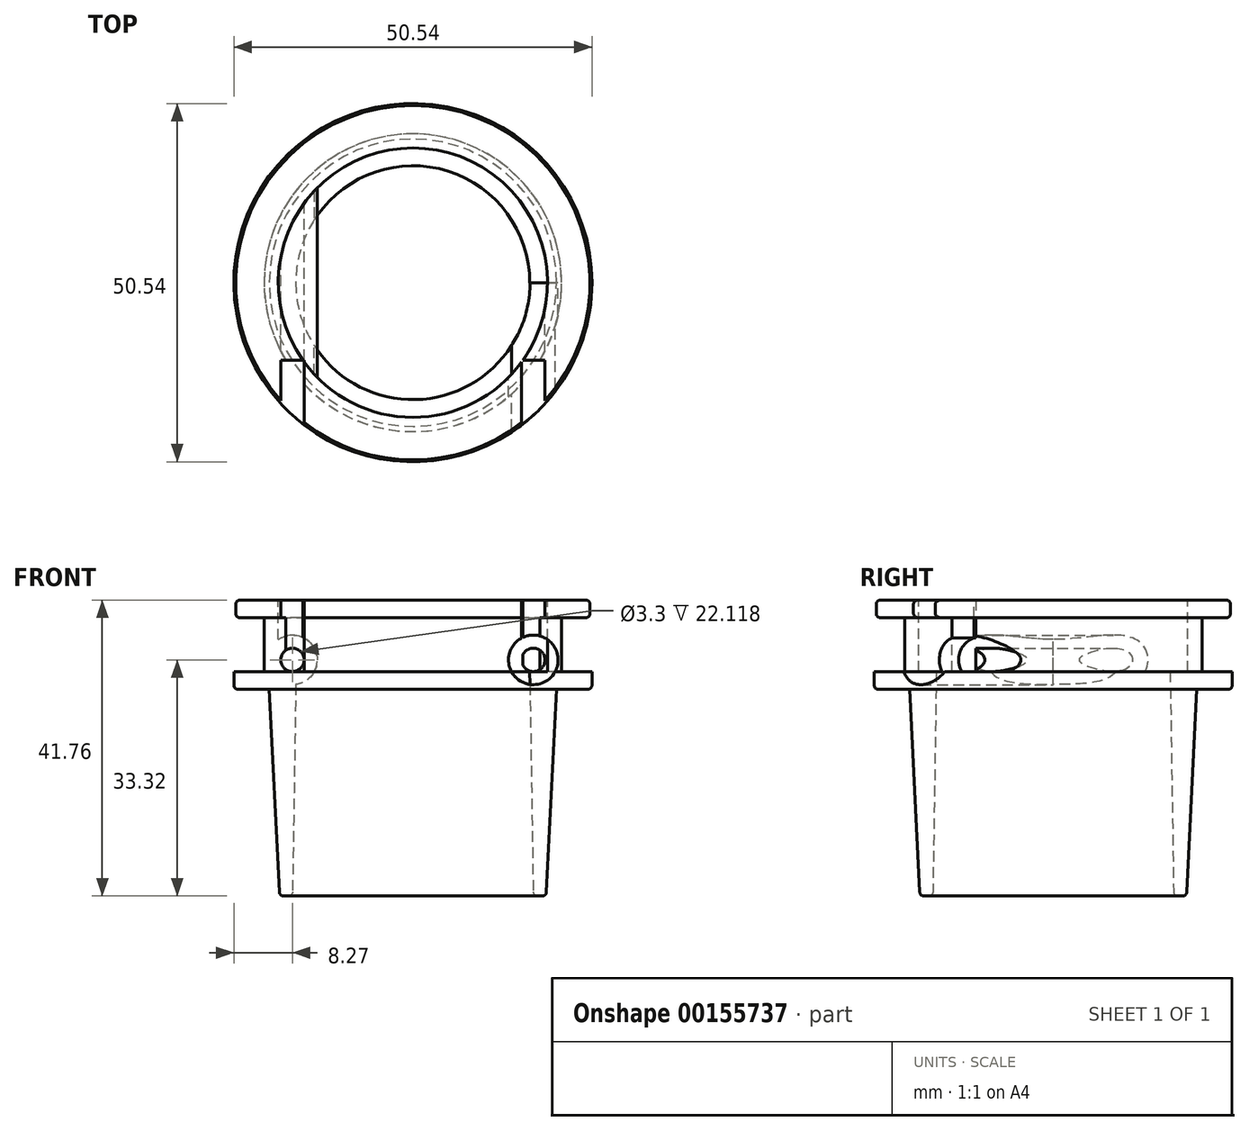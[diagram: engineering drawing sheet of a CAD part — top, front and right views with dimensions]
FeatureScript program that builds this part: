
annotation { "Feature Type Name" : "Feature", "Feature Type Description" : "" }
export const myFeature = defineFeature(function(context is Context, id is Id, definition is map)
    precondition{}
    {
        {
            var Q0;
            Q0=qCreatedBy(makeId("Front.planeOp"),FACE);
            var sketch = newSketch(context, id + "F0", { "sketchPlane" : qUnion([Q0])});
            skLineSegment(sketch, "E0", {"start": v(17, -31.67) * mm, "end": v(18.82, -31.67) * mm});
            skLineSegment(sketch, "E1", {"start": v(17, -31.67) * mm, "end": v(16.5, 0) * mm});
            skLineSegment(sketch, "E2", {"start": v(18.82, -31.67) * mm, "end": v(20.27, -2.5) * mm});
            skLineSegment(sketch, "E3", {"start": v(20.27, -2.5) * mm, "end": v(25.27, -2.5) * mm});
            skLineSegment(sketch, "E4", {"start": v(25.27, -2.5) * mm, "end": v(25.27, 0) * mm});
            skLineSegment(sketch, "E5", {"start": v(25.27, 0) * mm, "end": v(21, 0) * mm});
            skLineSegment(sketch, "E6", {"start": v(19, 0) * mm, "end": v(19, 10.1) * mm});
            skLineSegment(sketch, "E7", {"start": v(19, 10.1) * mm, "end": v(25, 10.1) * mm});
            skLineSegment(sketch, "E8", {"start": v(25, 10.1) * mm, "end": v(25, 7.6) * mm});
            skLineSegment(sketch, "E9", {"start": v(25, 7.6) * mm, "end": v(21, 7.6) * mm});
            skLineSegment(sketch, "E10", {"start": v(21, 7.6) * mm, "end": v(21, 0) * mm});
            skLineSegment(sketch, "E11.trimOffspring", {"start": v(19, 0) * mm, "end": v(16.5, 0) * mm});
            skLineSegment(sketch, "E12", {"start": v(0, 0) * mm, "end": v(0, -100.55) * mm, "construction": true});
            skSolve(sketch);
        }
        {
            var Q0;
            Q0 = qSketchRegion(id + "F0", true);
            var Q1;
            Q1=sQuery(id+"F0.wireOp",EDGE,"E12");
            revolve(context, id + "F1", {"entities" : qUnion([Q0]), "axis" : qUnion([Q1]), "revolveType" : RevolveType.FULL});
        }
        {
            var Q0;
            Q0=qCreatedBy(makeId("Front.planeOp"),FACE);
            var sketch = newSketch(context, id + "F2", { "sketchPlane" : qUnion([Q0])});
            skCircle(sketch, "E13", {"center": v(-17, 1.65) * mm, "radius": 1.65 * mm});
            skCircle(sketch, "E14", {"center": v(-17, 1.65) * mm, "radius": 3.5 * mm});
            skCircle(sketch, "E15.MirrorC", {"center": v(17, 1.65) * mm, "radius": 3.5 * mm});
            skCircle(sketch, "E16.MirrorC", {"center": v(17, 1.65) * mm, "radius": 1.65 * mm});
            skSolve(sketch);
        }
        {
            var Q0;
            Q0=makeQuery(id+"F2.imprint","IMPRINT",FACE,{"disambiguationData":[TD([[makeQuery(id+"F2.imprint","IMPRINT",EDGE,{"derivedFrom":sQuery(id+"F2.wireOp",EDGE,"E13")}),-1.0]])]});
            var Q1;
            Q1=makeQuery(id+"F2.imprint","IMPRINT",FACE,{"disambiguationData":[TD([[makeQuery(id+"F2.imprint","IMPRINT",EDGE,{"derivedFrom":sQuery(id+"F2.wireOp",EDGE,"E15.MirrorC")}),-1.0]])]});
            var Q2;
            Q2=makeQuery(id+"F1.opRevolve","SWEPT_FACE",FACE,{"disambiguationData":[OSD([sQuery(id+"F0.wireOp",EDGE,"E6")])]});
            var Q3;
            Q3=makeQuery(id+"F1.opRevolve","SWEPT_BODY",BODY,{"disambiguationData":[OSD([sQuery(id+"F0.wireOp",EDGE,"E0"),sQuery(id+"F0.wireOp",EDGE,"E1"),sQuery(id+"F0.wireOp",EDGE,"E2"),sQuery(id+"F0.wireOp",EDGE,"E3"),sQuery(id+"F0.wireOp",EDGE,"E4"),sQuery(id+"F0.wireOp",EDGE,"E5"),sQuery(id+"F0.wireOp",EDGE,"E6"),sQuery(id+"F0.wireOp",EDGE,"E7"),sQuery(id+"F0.wireOp",EDGE,"E8"),sQuery(id+"F0.wireOp",EDGE,"E9"),sQuery(id+"F0.wireOp",EDGE,"E10"),sQuery(id+"F0.wireOp",EDGE,"E11.trimOffspring")])]});
            extrude(context, id + "F3", {"entities" : qUnion([Q0, Q1]), "operationType" : NewBodyOperationType.ADD, "endBound" : BoundingType.UP_TO_SURFACE, "endBoundEntityFace" : qUnion([Q2]), "endBoundEntityBody" : qUnion([Q3]), "depth" : 25 * mm});
        }
        {
            var Q0;
            Q0=makeQuery(id+"F2.imprint","IMPRINT",FACE,{"disambiguationData":[TD([[makeQuery(id+"F2.imprint","IMPRINT",EDGE,{"derivedFrom":sQuery(id+"F2.wireOp",EDGE,"E13")}),-1.0]])]});
            var Q1;
            Q1=makeQuery(id+"F2.imprint","IMPRINT",FACE,{"disambiguationData":[TD([[makeQuery(id+"F2.imprint","IMPRINT",EDGE,{"derivedFrom":sQuery(id+"F2.wireOp",EDGE,"E15.MirrorC")}),-1.0]])]});
            var Q2;
            Q2=makeQuery(id+"F3.boolean.opBoolean","SPLIT",FACE,{"disambiguationData":[TD([makeQuery(id+"F1.opRevolve","SWEPT_FACE",FACE,{"disambiguationData":[OSD([sQuery(id+"F0.wireOp",EDGE,"E7")])]})])],"derivedFrom":makeQuery(id+"F1.opRevolve","SWEPT_FACE",FACE,{"disambiguationData":[OSD([sQuery(id+"F0.wireOp",EDGE,"E6")])]})});
            extrude(context, id + "F4", {"entities" : qUnion([Q0, Q1]), "operationType" : NewBodyOperationType.ADD, "endBound" : BoundingType.UP_TO_SURFACE, "oppositeDirection" : true, "endBoundEntityFace" : qUnion([Q2]), "depth" : 25 * mm});
        }
        {
            var Q0;
            Q0=qCreatedBy(makeId("Front.planeOp"),FACE);
            cPlane(context, id + "F5", {"entities" : qUnion([Q0]), "cplaneType" : CPlaneType.OFFSET, "offset" : (21.84 / 2) * mm, "width" : 150 * mm, "height" : 150 * mm});
        }
        {
            var Q0;
            Q0=qCreatedBy(id+"F5.planeOp",FACE);
            var sketch = newSketch(context, id + "F6", { "sketchPlane" : qUnion([Q0])});
            skLineSegment(sketch, "E17.bottom", {"start": v(-18.65, 10.1) * mm, "end": v(-15.35, 10.1) * mm});
            skLineSegment(sketch, "E17.top", {"start": v(-18.65, 0) * mm, "end": v(-15.35, 0) * mm});
            skLineSegment(sketch, "E17.left", {"start": v(-18.65, 10.1) * mm, "end": v(-18.65, 0) * mm});
            skLineSegment(sketch, "E17.right", {"start": v(-15.35, 10.1) * mm, "end": v(-15.35, 0) * mm});
            skLineSegment(sketch, "E18.MirrorCS", {"start": v(18.65, 10.1) * mm, "end": v(18.65, 0) * mm});
            skLineSegment(sketch, "E19.MirrorCS", {"start": v(18.65, 0) * mm, "end": v(15.35, 0) * mm});
            skLineSegment(sketch, "E20.MirrorCS", {"start": v(15.35, 10.1) * mm, "end": v(15.35, 0) * mm});
            skLineSegment(sketch, "E21.MirrorCS", {"start": v(18.65, 10.1) * mm, "end": v(15.35, 10.1) * mm});
            skSolve(sketch);
        }
        {
            var Q0;
            Q0 = qSketchRegion(id + "F6", true);
            extrude(context, id + "F7", {"entities" : qUnion([Q0]), "operationType" : NewBodyOperationType.REMOVE, "depth" : 10.7 * mm});
        }
        {
            var Q0;
            Q0=makeQuery(id+"F2.imprint","IMPRINT",FACE,{"disambiguationData":[TD([[makeQuery(id+"F2.imprint","IMPRINT",EDGE,{"derivedFrom":sQuery(id+"F2.wireOp",EDGE,"E16.MirrorC")}),-1.0]])]});
            var Q1;
            Q1=makeQuery(id+"F2.imprint","IMPRINT",FACE,{"disambiguationData":[TD([[makeQuery(id+"F2.imprint","IMPRINT",EDGE,{"derivedFrom":sQuery(id+"F2.wireOp",EDGE,"E13")}),1.0]])]});
            var Q2;
            Q2=sQuery(id+"F2.wireOp",EDGE,"E13");
            extrude(context, id + "F8", {"entities" : qUnion([Q0, Q1]), "operationType" : NewBodyOperationType.REMOVE, "surfaceEntities" : qUnion([Q2]), "depth" : 25 * mm});
        }
        {
            var Q0;
            Q0=makeQuery(id+"F1.opRevolve","SWEPT_EDGE",EDGE,{"disambiguationData":[OSD([sQuery(id+"F0.wireOp",EDGE,"E0"),sQuery(id+"F0.wireOp",EDGE,"E2")])]});
            var Q1;
            Q1=makeQuery(id+"F1.opRevolve","SWEPT_EDGE",EDGE,{"disambiguationData":[OSD([sQuery(id+"F0.wireOp",EDGE,"E0"),sQuery(id+"F0.wireOp",EDGE,"E1")])]});
            var Q2;
            Q2=makeQuery(id+"F1.opRevolve","SWEPT_EDGE",EDGE,{"disambiguationData":[OSD([sQuery(id+"F0.wireOp",EDGE,"E3"),sQuery(id+"F0.wireOp",EDGE,"E4")])]});
            var Q3;
            Q3=makeQuery(id+"F7.boolean.opBoolean","INTERSECT",EDGE,{"derivedFrom":[makeQuery(id+"F7.opExtrude","SWEPT_FACE",FACE,{"disambiguationData":[OSD([sQuery(id+"F6.wireOp",EDGE,"E17.top")])]}),makeQuery(id+"F7.opExtrude","SWEPT_FACE",FACE,{"disambiguationData":[OSD([sQuery(id+"F6.wireOp",EDGE,"E19.MirrorCS")])]})]});
            var Q4;
            {var subQ0=sQuery(id+"F0.wireOp",EDGE,"E8");var subQ1=sQuery(id+"F0.wireOp",EDGE,"E9");Q4=makeQuery(id+"F7.boolean.opBoolean","SPLIT",EDGE,{"disambiguationData":[TD([makeQuery(id+"F7.opExtrude","SWEPT_FACE",FACE,{"disambiguationData":[OSD([sQuery(id+"F6.wireOp",EDGE,"E17.left")])]})])],"derivedFrom":makeQuery(id+"F1.opRevolve","SWEPT_EDGE",EDGE,{"disambiguationData":[OSD([subQ0,subQ1])]})});}
            var Q5;
            {var subQ0=sQuery(id+"F0.wireOp",EDGE,"E7");var subQ1=sQuery(id+"F0.wireOp",EDGE,"E8");Q5=makeQuery(id+"F7.boolean.opBoolean","SPLIT",EDGE,{"disambiguationData":[TD([makeQuery(id+"F7.opExtrude","SWEPT_FACE",FACE,{"disambiguationData":[OSD([sQuery(id+"F6.wireOp",EDGE,"E17.left")])]})])],"derivedFrom":makeQuery(id+"F1.opRevolve","SWEPT_EDGE",EDGE,{"disambiguationData":[OSD([subQ0,subQ1])]})});}
            var Q6;
            {var subQ0=sQuery(id+"F0.wireOp",EDGE,"E7");var subQ1=sQuery(id+"F0.wireOp",EDGE,"E8");Q6=makeQuery(id+"F7.boolean.opBoolean","SPLIT",EDGE,{"disambiguationData":[TD([makeQuery(id+"F7.opExtrude","SWEPT_FACE",FACE,{"disambiguationData":[OSD([sQuery(id+"F6.wireOp",EDGE,"E17.right")])]})])],"derivedFrom":makeQuery(id+"F1.opRevolve","SWEPT_EDGE",EDGE,{"disambiguationData":[OSD([subQ0,subQ1])]})});}
            var Q7;
            {var subQ0=sQuery(id+"F0.wireOp",EDGE,"E8");var subQ1=sQuery(id+"F0.wireOp",EDGE,"E9");Q7=makeQuery(id+"F7.boolean.opBoolean","SPLIT",EDGE,{"disambiguationData":[TD([makeQuery(id+"F7.opExtrude","SWEPT_FACE",FACE,{"disambiguationData":[OSD([sQuery(id+"F6.wireOp",EDGE,"E17.right")])]})])],"derivedFrom":makeQuery(id+"F1.opRevolve","SWEPT_EDGE",EDGE,{"disambiguationData":[OSD([subQ0,subQ1])]})});}
            fillet(context, id + "F9", {"entities" : qUnion([Q0, Q1, Q2, Q3, Q4, Q5, Q6, Q7]), "radius" : 0.6 * mm, "tangentPropagation" : true, "allowEdgeOverflow" : false});
        }
    });
